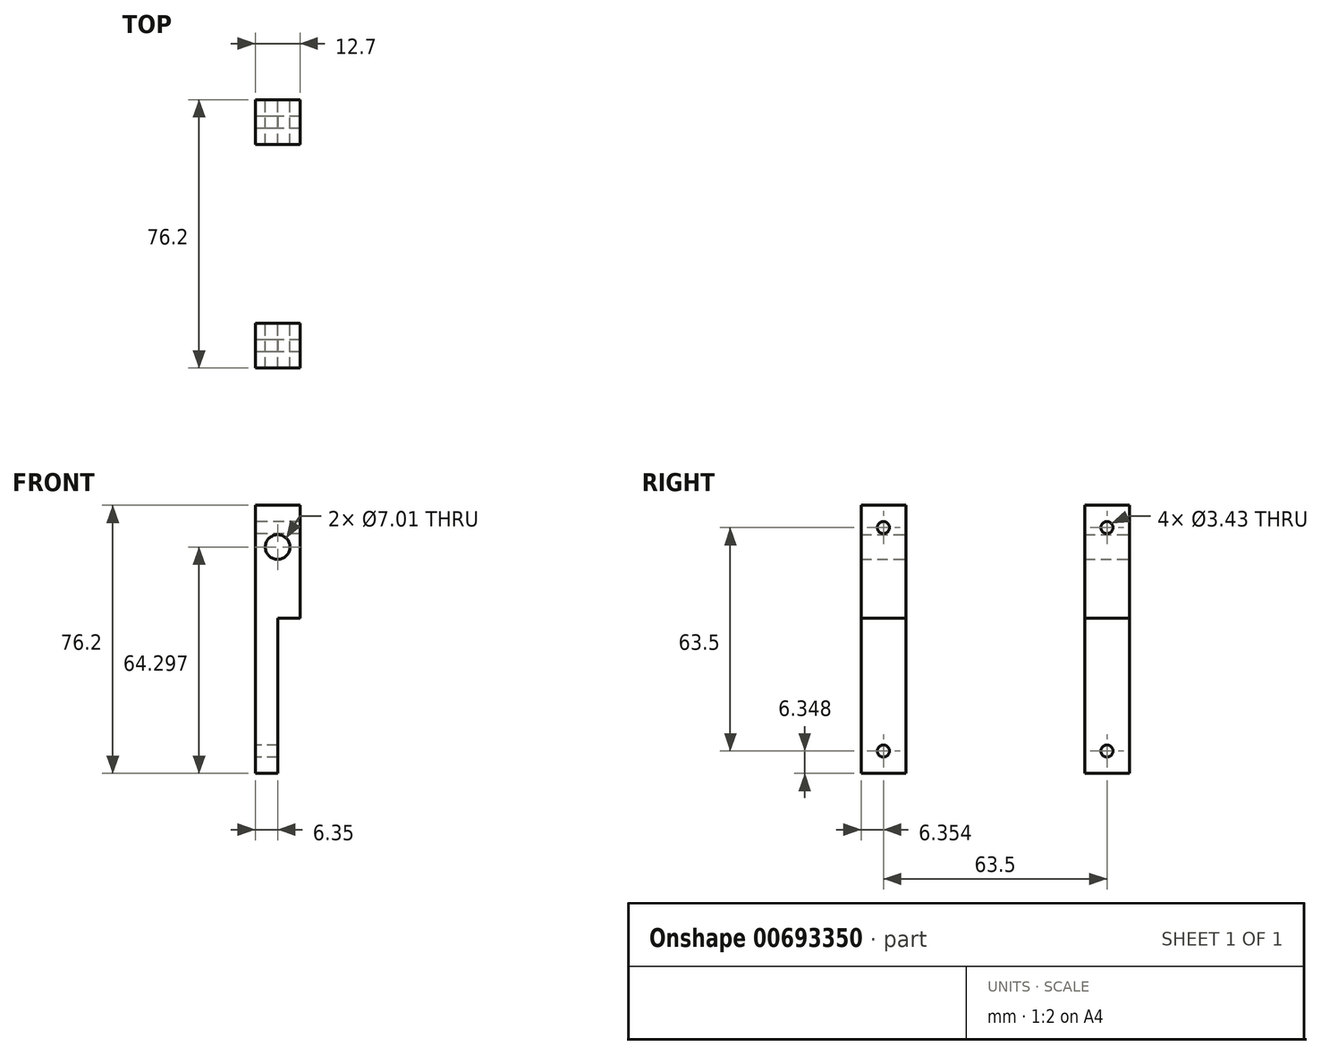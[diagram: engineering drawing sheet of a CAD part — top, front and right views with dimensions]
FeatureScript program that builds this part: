
annotation { "Feature Type Name" : "Feature", "Feature Type Description" : "" }
export const myFeature = defineFeature(function(context is Context, id is Id, definition is map)
    precondition{}
    {
        {
            var Q0;
            Q0=qCreatedBy(makeId("Right.planeOp"),FACE);
            var sketch = newSketch(context, id + "F0", { "sketchPlane" : qUnion([Q0])});
            skLineSegment(sketch, "E0.bottom", {"start": v(-50.07, 46.14) * mm, "end": v(-37.37, 46.14) * mm});
            skLineSegment(sketch, "E0.top", {"start": v(-50.07, -30.06) * mm, "end": v(-37.37, -30.06) * mm});
            skLineSegment(sketch, "E0.left", {"start": v(-50.07, 46.14) * mm, "end": v(-50.07, -30.06) * mm});
            skLineSegment(sketch, "E0.right", {"start": v(-37.37, 46.14) * mm, "end": v(-37.37, -30.06) * mm});
            skLineSegment(sketch, "E1.bottom", {"start": v(13.43, 46.14) * mm, "end": v(26.13, 46.14) * mm});
            skLineSegment(sketch, "E1.top", {"start": v(13.43, -30.06) * mm, "end": v(26.13, -30.06) * mm});
            skLineSegment(sketch, "E1.left", {"start": v(13.43, 46.14) * mm, "end": v(13.43, -30.06) * mm});
            skLineSegment(sketch, "E1.right", {"start": v(26.13, 46.14) * mm, "end": v(26.13, -30.06) * mm});
            skCircle(sketch, "E2", {"center": v(-43.72, 39.79) * mm, "radius": 1.71 * mm});
            skCircle(sketch, "E3", {"center": v(19.78, 39.79) * mm, "radius": 1.71 * mm});
            skCircle(sketch, "E4", {"center": v(-43.72, -23.71) * mm, "radius": 1.71 * mm});
            skCircle(sketch, "E5", {"center": v(19.78, -23.71) * mm, "radius": 1.71 * mm});
            skLineSegment(sketch, "E6.bottom", {"start": v(13.43, 14.02) * mm, "end": v(26.13, 14.02) * mm});
            skLineSegment(sketch, "E6.top", {"start": v(13.43, -51.76) * mm, "end": v(26.13, -51.76) * mm});
            skLineSegment(sketch, "E6.left", {"start": v(13.43, 14.02) * mm, "end": v(13.43, -51.76) * mm});
            skLineSegment(sketch, "E6.right", {"start": v(26.13, 14.02) * mm, "end": v(26.13, -51.76) * mm});
            skPoint(sketch, "E7.firstSnap0", {"position": v(-37.37, 8.04) * mm});
            skPoint(sketch, "E7.oppositeSnap0", {"position": v(-50.07, 8.04) * mm});
            skLineSegment(sketch, "E7.bottom", {"start": v(-37.37, 14.02) * mm, "end": v(-50.07, 14.02) * mm});
            skLineSegment(sketch, "E7.top", {"start": v(-37.37, -51.76) * mm, "end": v(-50.07, -51.76) * mm});
            skLineSegment(sketch, "E7.left", {"start": v(-37.37, 14.02) * mm, "end": v(-37.37, -51.76) * mm});
            skLineSegment(sketch, "E7.right", {"start": v(-50.07, 14.02) * mm, "end": v(-50.07, -51.76) * mm});
            skSolve(sketch);
        }
        {
            var Q0;
            Q0=makeQuery(id+"F0.imprint","IMPRINT",FACE,{"disambiguationData":[TD([[makeQuery(id+"F0.imprint","IMPRINT",EDGE,{"derivedFrom":sQuery(id+"F0.wireOp",EDGE,"E0.bottom")}),-1.0]])]});
            var Q1;
            Q1=makeQuery(id+"F0.imprint","IMPRINT",FACE,{"disambiguationData":[TD([[makeQuery(id+"F0.imprint","IMPRINT",EDGE,{"derivedFrom":sQuery(id+"F0.wireOp",EDGE,"E1.bottom")}),-1.0]])]});
            var Q2;
            {var subQ2=sQuery(id+"F0.wireOp",EDGE,"E0.top");Q2=makeQuery(id+"F0.imprint","IMPRINT",FACE,{"disambiguationData":[TD([[makeQuery(id+"F0.imprint","IMPRINT",EDGE,{"derivedFrom":subQ2}),1.0]])]});}
            var Q3;
            {var subQ1=sQuery(id+"F0.wireOp",EDGE,"E1.top");Q3=makeQuery(id+"F0.imprint","IMPRINT",FACE,{"disambiguationData":[TD([[makeQuery(id+"F0.imprint","IMPRINT",EDGE,{"derivedFrom":subQ1}),1.0]])]});}
            extrude(context, id + "F1", {"entities" : qUnion([Q0, Q1, Q2, Q3]), "endBound" : BoundingType.SYMMETRIC, "depth" : 12.7 * mm, "offsetDistance" : 25.4 * mm});
        }
        {
            var Q0;
            Q0=qCreatedBy(makeId("Front.planeOp"),FACE);
            var sketch = newSketch(context, id + "F2", { "sketchPlane" : qUnion([Q0])});
            skCircle(sketch, "E8", {"center": v(0, 34.24) * mm, "radius": 3.5 * mm});
            skSolve(sketch);
        }
        {
            var Q0;
            Q0 = qSketchRegion(id + "F2", true);
            extrude(context, id + "F3", {"entities" : qUnion([Q0]), "endBound" : BoundingType.SYMMETRIC, "depth" : 101.6 * mm, "offsetDistance" : 25.4 * mm});
        }
        {
            var Q0;
            Q0=makeQuery(id+"F3.opExtrude","SWEPT_BODY",BODY,{"disambiguationData":[OSD([sQuery(id+"F2.wireOp",EDGE,"E8")])]});
            var Q1;
            Q1=makeQuery(id+"F1.opExtrude","SWEPT_BODY",BODY,{"disambiguationData":[OSD([sQuery(id+"F0.wireOp",EDGE,"E1.bottom"),sQuery(id+"F0.wireOp",EDGE,"E1.top"),sQuery(id+"F0.wireOp",EDGE,"E1.left"),sQuery(id+"F0.wireOp",EDGE,"E1.right"),sQuery(id+"F0.wireOp",EDGE,"E3")])]});
            var Q2;
            Q2=makeQuery(id+"F1.opExtrude","SWEPT_BODY",BODY,{"disambiguationData":[OSD([sQuery(id+"F0.wireOp",EDGE,"E0.bottom"),sQuery(id+"F0.wireOp",EDGE,"E0.top"),sQuery(id+"F0.wireOp",EDGE,"E0.left"),sQuery(id+"F0.wireOp",EDGE,"E0.right"),sQuery(id+"F0.wireOp",EDGE,"E2")])]});
            booleanBodies(context, id + "F4", {"operationType" : BooleanOperationType.SUBTRACTION, "tools" : qUnion([Q0]), "targets" : qUnion([Q1, Q2])});
        }
        {
            var Q0;
            {var subQ2=sQuery(id+"F0.wireOp",EDGE,"E0.top");Q0=makeQuery(id+"F0.imprint","IMPRINT",FACE,{"disambiguationData":[TD([[makeQuery(id+"F0.imprint","IMPRINT",EDGE,{"derivedFrom":subQ2}),1.0]])]});}
            var Q1;
            {var subQ1=sQuery(id+"F0.wireOp",EDGE,"E1.top");Q1=makeQuery(id+"F0.imprint","IMPRINT",FACE,{"disambiguationData":[TD([[makeQuery(id+"F0.imprint","IMPRINT",EDGE,{"derivedFrom":subQ1}),1.0]])]});}
            var Q2;
            {var subQ0=sQuery(id+"F0.wireOp",EDGE,"E1.top");Q2=makeQuery(id+"F0.imprint","IMPRINT",FACE,{"disambiguationData":[TD([[makeQuery(id+"F0.imprint","IMPRINT",EDGE,{"derivedFrom":subQ0}),-1.0]])]});}
            var Q3;
            {var subQ0=sQuery(id+"F0.wireOp",EDGE,"E0.top");Q3=makeQuery(id+"F0.imprint","IMPRINT",FACE,{"disambiguationData":[TD([[makeQuery(id+"F0.imprint","IMPRINT",EDGE,{"derivedFrom":subQ0}),-1.0]])]});}
            extrude(context, id + "F5", {"entities" : qUnion([Q0, Q1, Q2, Q3]), "depth" : 25.4 * mm, "offsetDistance" : 25.4 * mm});
        }
        {
            var Q0;
            Q0=makeQuery(id+"F5.opExtrude","SWEPT_BODY",BODY,{"disambiguationData":[OSD([sQuery(id+"F0.wireOp",EDGE,"E5"),sQuery(id+"F0.wireOp",EDGE,"E6.bottom"),sQuery(id+"F0.wireOp",EDGE,"E6.top"),sQuery(id+"F0.wireOp",EDGE,"E6.left"),sQuery(id+"F0.wireOp",EDGE,"E6.right")])]});
            var Q1;
            Q1=makeQuery(id+"F5.opExtrude","SWEPT_BODY",BODY,{"disambiguationData":[OSD([sQuery(id+"F0.wireOp",EDGE,"E4"),sQuery(id+"F0.wireOp",EDGE,"E7.bottom"),sQuery(id+"F0.wireOp",EDGE,"E7.top"),sQuery(id+"F0.wireOp",EDGE,"E7.left"),sQuery(id+"F0.wireOp",EDGE,"E7.right")])]});
            var Q2;
            Q2=makeQuery(id+"F1.opExtrude","SWEPT_BODY",BODY,{"disambiguationData":[OSD([sQuery(id+"F0.wireOp",EDGE,"E1.bottom"),sQuery(id+"F0.wireOp",EDGE,"E1.top"),sQuery(id+"F0.wireOp",EDGE,"E1.left"),sQuery(id+"F0.wireOp",EDGE,"E1.right"),sQuery(id+"F0.wireOp",EDGE,"E3"),sQuery(id+"F0.wireOp",EDGE,"E5"),sQuery(id+"F0.wireOp",EDGE,"E6.left"),sQuery(id+"F0.wireOp",EDGE,"E6.right")])]});
            var Q3;
            Q3=makeQuery(id+"F1.opExtrude","SWEPT_BODY",BODY,{"disambiguationData":[OSD([sQuery(id+"F0.wireOp",EDGE,"E0.bottom"),sQuery(id+"F0.wireOp",EDGE,"E0.top"),sQuery(id+"F0.wireOp",EDGE,"E0.left"),sQuery(id+"F0.wireOp",EDGE,"E0.right"),sQuery(id+"F0.wireOp",EDGE,"E2"),sQuery(id+"F0.wireOp",EDGE,"E4"),sQuery(id+"F0.wireOp",EDGE,"E7.left"),sQuery(id+"F0.wireOp",EDGE,"E7.right")])]});
            booleanBodies(context, id + "F6", {"operationType" : BooleanOperationType.SUBTRACTION, "tools" : qUnion([Q0, Q1]), "targets" : qUnion([Q2, Q3])});
        }
    });
